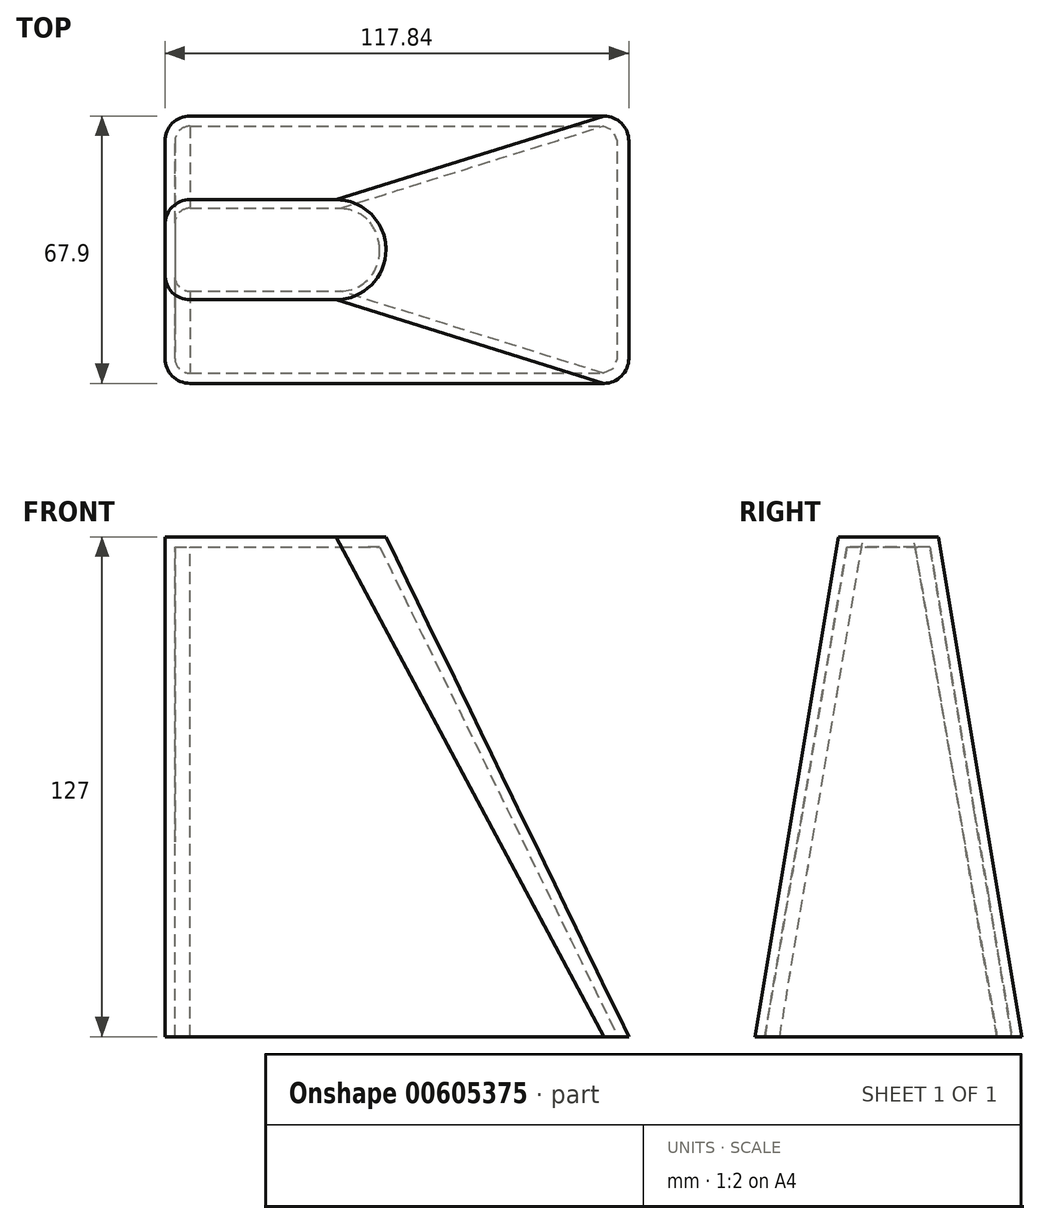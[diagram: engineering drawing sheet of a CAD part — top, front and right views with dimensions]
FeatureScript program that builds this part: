
annotation { "Feature Type Name" : "Feature", "Feature Type Description" : "" }
export const myFeature = defineFeature(function(context is Context, id is Id, definition is map)
    precondition{}
    {
        {
            var Q0;
            Q0=qCreatedBy(makeId("Top.planeOp"),FACE);
            var sketch = newSketch(context, id + "F0", { "sketchPlane" : qUnion([Q0])});
            skLineSegment(sketch, "E0.bottom", {"start": v(-52.57, 33.95) * mm, "end": v(52.57, 33.95) * mm});
            skLineSegment(sketch, "E0.top", {"start": v(-52.57, -33.95) * mm, "end": v(52.57, -33.95) * mm});
            skLineSegment(sketch, "E0.left", {"start": v(-58.92, 27.6) * mm, "end": v(-58.92, -27.6) * mm});
            skLineSegment(sketch, "E0.right", {"start": v(58.92, 27.6) * mm, "end": v(58.92, -27.6) * mm});
            skPoint(sketch, "E0.middle", {"position": v(0, 0) * mm});
            skPoint(sketch, "E1.visualSharp", {"position": v(-58.92, 33.95) * mm});
            skArc(sketch, "E1.filletArc", {"start": v(-52.57, 33.95) * mm, "mid": v(-57.06, 32.1) * mm, "end": v(-58.92, 27.6) * mm});
            skPoint(sketch, "E2.visualSharp", {"position": v(58.92, 33.95) * mm});
            skArc(sketch, "E2.filletArc", {"start": v(58.92, 27.6) * mm, "mid": v(57.06, 32.1) * mm, "end": v(52.57, 33.95) * mm});
            skPoint(sketch, "E3.visualSharp", {"position": v(58.92, -33.95) * mm});
            skArc(sketch, "E3.filletArc", {"start": v(52.57, -33.95) * mm, "mid": v(57.06, -32.1) * mm, "end": v(58.92, -27.6) * mm});
            skPoint(sketch, "E4.visualSharp", {"position": v(-58.92, -33.95) * mm});
            skArc(sketch, "E4.filletArc", {"start": v(-58.92, -27.6) * mm, "mid": v(-57.06, -32.1) * mm, "end": v(-52.57, -33.95) * mm});
            skSolve(sketch);
        }
        {
            var Q0;
            Q0=qCreatedBy(makeId("Top.planeOp"),FACE);
            cPlane(context, id + "F1", {"entities" : qUnion([Q0]), "cplaneType" : CPlaneType.OFFSET, "offset" : 127 * mm, "width" : 152.4 * mm, "height" : 152.4 * mm});
        }
        {
            var Q0;
            Q0=qCreatedBy(id+"F1.planeOp",FACE);
            var sketch = newSketch(context, id + "F2", { "sketchPlane" : qUnion([Q0])});
            skLineSegment(sketch, "E5.bottom", {"start": v(-52.57, 12.7) * mm, "end": v(-15.47, 12.7) * mm});
            skLineSegment(sketch, "E5.top", {"start": v(-52.57, -12.7) * mm, "end": v(-15.47, -12.7) * mm});
            skLineSegment(sketch, "E5.left", {"start": v(-58.92, 6.35) * mm, "end": v(-58.92, -6.35) * mm});
            skLineSegment(sketch, "E5.right", {"start": v(-2.77, 0) * mm, "end": v(-2.77, 0) * mm});
            skPoint(sketch, "E6.visualSharp", {"position": v(-2.77, 12.7) * mm});
            skArc(sketch, "E6.filletArc", {"start": v(-2.77, 0) * mm, "mid": v(-6.5, 8.98) * mm, "end": v(-15.47, 12.7) * mm});
            skPoint(sketch, "E7.visualSharp", {"position": v(-2.77, -12.7) * mm});
            skArc(sketch, "E7.filletArc", {"start": v(-15.47, -12.7) * mm, "mid": v(-6.5, -8.98) * mm, "end": v(-2.77, 0) * mm});
            skPoint(sketch, "E8.visualSharp", {"position": v(-58.92, 12.7) * mm});
            skArc(sketch, "E8.filletArc", {"start": v(-52.57, 12.7) * mm, "mid": v(-57.06, 10.84) * mm, "end": v(-58.92, 6.35) * mm});
            skPoint(sketch, "E9.visualSharp", {"position": v(-58.92, -12.7) * mm});
            skArc(sketch, "E9.filletArc", {"start": v(-58.92, -6.35) * mm, "mid": v(-57.06, -10.84) * mm, "end": v(-52.57, -12.7) * mm});
            skSolve(sketch);
        }
        {
            var Q0;
            Q0=makeQuery(id+"F0.imprint","IMPRINT",FACE,{"disambiguationData":[TD([[makeQuery(id+"F0.imprint","IMPRINT",EDGE,{"derivedFrom":sQuery(id+"F0.wireOp",EDGE,"E0.bottom")}),-1.0]])]});
            var Q1;
            Q1=makeQuery(id+"F2.imprint","IMPRINT",FACE,{"disambiguationData":[TD([[makeQuery(id+"F2.imprint","IMPRINT",EDGE,{"derivedFrom":sQuery(id+"F2.wireOp",EDGE,"E5.bottom")}),-1.0]])]});
            loft(context, id + "F3", {"sheetProfilesArray" : [{ "sheetProfileEntities" : qUnion([Q0]) }, { "sheetProfileEntities" : qUnion([Q1]) }]});
        }
        {
            var Q0;
            Q0=makeQuery(id+"F3.opLoft","CAP_FACE",FACE,{"disambiguationData":[OSD([makeQuery(id+"F0.imprint","IMPRINT",FACE,{"disambiguationData":[TD([[makeQuery(id+"F0.imprint","IMPRINT",EDGE,{"derivedFrom":sQuery(id+"F0.wireOp",EDGE,"E0.bottom")}),-1.0]])]})])],"isStart":true});
            shell(context, id + "F4", {"entities" : qUnion([Q0]), "thickness" : 2.54 * mm});
        }
    });
